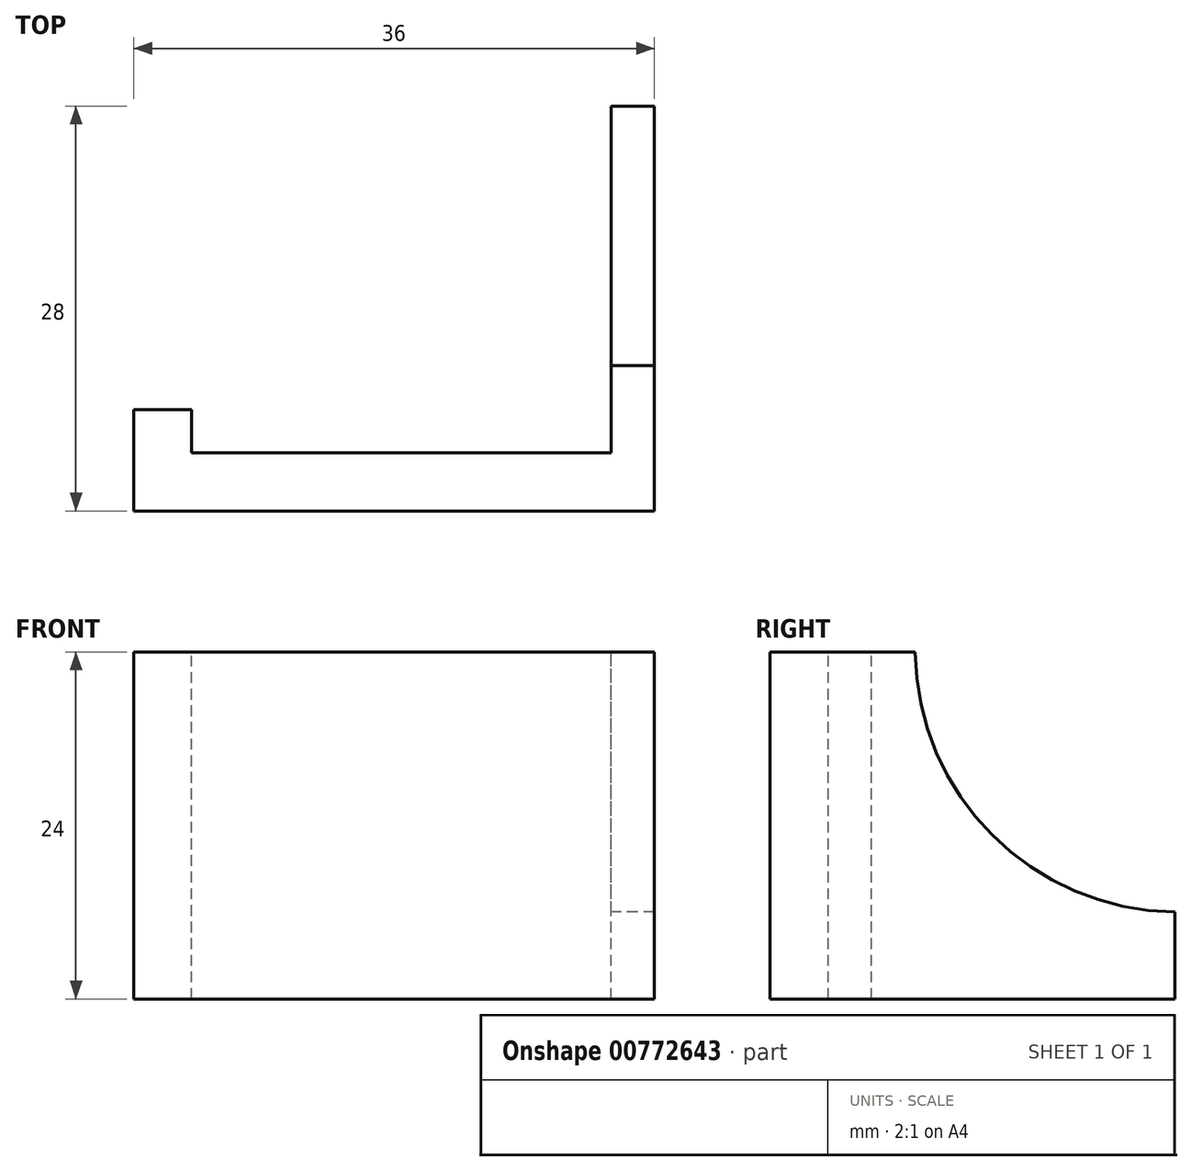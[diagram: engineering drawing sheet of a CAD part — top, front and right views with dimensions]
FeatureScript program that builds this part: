
annotation { "Feature Type Name" : "Feature", "Feature Type Description" : "" }
export const myFeature = defineFeature(function(context is Context, id is Id, definition is map)
    precondition{}
    {
        {
            var Q0;
            Q0=qCreatedBy(makeId("Right.planeOp"),FACE);
            var sketch = newSketch(context, id + "F0", { "sketchPlane" : qUnion([Q0])});
            skLineSegment(sketch, "E0", {"start": v(-23.8, 44.3) * mm, "end": v(0.2, 44.3) * mm});
            skLineSegment(sketch, "E1", {"start": v(-23.8, 44.3) * mm, "end": v(-23.8, 20.3) * mm});
            skLineSegment(sketch, "E2", {"start": v(-23.8, 20.3) * mm, "end": v(-19.76, 20.3) * mm});
            skLineSegment(sketch, "E3", {"start": v(-19.76, 20.3) * mm, "end": v(-17.76, 20.3) * mm});
            skLineSegment(sketch, "E4", {"start": v(0.2, 44.3) * mm, "end": v(0.2, 38.28) * mm});
            skArc(sketch, "E5", {"start": v(0.2, 38.28) * mm, "mid": v(-12.44, 32.94) * mm, "end": v(-17.76, 20.3) * mm});
            skSolve(sketch);
        }
        {
            var Q0;
            Q0=makeQuery(id+"F0.imprint","IMPRINT",FACE,{"disambiguationData":[TD([[makeQuery(id+"F0.imprint","IMPRINT",EDGE,{"derivedFrom":sQuery(id+"F0.wireOp",EDGE,"E0")}),-1.0]])]});
            extrude(context, id + "F1", {"entities" : qUnion([Q0]), "depth" : 3 * mm, "offsetDistance" : 25 * mm});
        }
        {
            var Q0;
            Q0=makeQuery(id+"F1.opExtrude","SWEPT_FACE",FACE,{"disambiguationData":[OSD([sQuery(id+"F0.wireOp",EDGE,"E1")])]});
            extrude(context, id + "F2", {"entities" : qUnion([Q0]), "operationType" : NewBodyOperationType.ADD, "depth" : 4 * mm, "offsetDistance" : 25 * mm});
        }
        {
            var Q0;
            {var subQ0=sQuery(id+"F0.wireOp",EDGE,"E1");Q0=makeQuery(id+"F2.boolean.opBoolean","MERGE",FACE,{"derivedFrom":[makeQuery(id+"F1.opExtrude","CAP_FACE",FACE,{"disambiguationData":[OSD([sQuery(id+"F0.wireOp",EDGE,"E0"),subQ0,sQuery(id+"F0.wireOp",EDGE,"E2"),sQuery(id+"F0.wireOp",EDGE,"hRtY1aQG-A8Zh-szPu-RmAq-oDse8q4H1be6"),sQuery(id+"F0.wireOp",EDGE,"Tq682J4d-pl9S-xHzb-lzca-EFFe5oxrAv54")])],"isStart":true}),makeQuery(id+"F2.opExtrude","SWEPT_FACE",FACE,{"disambiguationData":[OSD([subQ0]),TDD([makeQuery(id+"F1.opExtrude","CAP_EDGE",EDGE,{"disambiguationData":[OSD([subQ0])],"isStart":true})])]})]});}
            var sketch = newSketch(context, id + "F3", { "sketchPlane" : qUnion([Q0])});
            skLineSegment(sketch, "E6.bottom", {"start": v(27.8, 44.3) * mm, "end": v(23.78, 44.3) * mm});
            skLineSegment(sketch, "E6.top", {"start": v(27.8, 20.3) * mm, "end": v(23.78, 20.3) * mm});
            skLineSegment(sketch, "E6.left", {"start": v(27.8, 44.3) * mm, "end": v(27.8, 20.3) * mm});
            skLineSegment(sketch, "E6.right", {"start": v(23.78, 44.3) * mm, "end": v(23.78, 20.3) * mm});
            skSolve(sketch);
        }
        {
            var Q0;
            Q0=makeQuery(id+"F3.imprint","IMPRINT",FACE,{"disambiguationData":[TD([[makeQuery(id+"F3.imprint","IMPRINT",EDGE,{"derivedFrom":sQuery(id+"F3.wireOp",EDGE,"E6.bottom")}),1.0]])]});
            extrude(context, id + "F4", {"entities" : qUnion([Q0]), "operationType" : NewBodyOperationType.ADD, "depth" : 29 * mm, "offsetDistance" : 25 * mm});
        }
        {
            var Q0;
            Q0=makeQuery(id+"F4.opExtrude","CAP_FACE",FACE,{"disambiguationData":[OSD([sQuery(id+"F3.wireOp",EDGE,"E6.bottom"),sQuery(id+"F3.wireOp",EDGE,"E6.top"),sQuery(id+"F3.wireOp",EDGE,"E6.left"),sQuery(id+"F3.wireOp",EDGE,"E6.right")])],"isStart":false});
            extrude(context, id + "F5", {"entities" : qUnion([Q0]), "operationType" : NewBodyOperationType.ADD, "depth" : 4 * mm, "offsetDistance" : 25 * mm});
        }
        {
            var Q0;
            {var subQ0=sQuery(id+"F3.wireOp",EDGE,"E6.right");Q0=makeQuery(id+"F5.boolean.opBoolean","MERGE",FACE,{"derivedFrom":[makeQuery(id+"F4.opExtrude","SWEPT_FACE",FACE,{"disambiguationData":[OSD([subQ0])]}),makeQuery(id+"F5.opExtrude","SWEPT_FACE",FACE,{"disambiguationData":[OSD([subQ0])]})]});}
            var sketch = newSketch(context, id + "F6", { "sketchPlane" : qUnion([Q0])});
            skLineSegment(sketch, "E7.bottom", {"start": v(33, 44.3) * mm, "end": v(29, 44.3) * mm});
            skLineSegment(sketch, "E7.top", {"start": v(33, 20.3) * mm, "end": v(29, 20.3) * mm});
            skLineSegment(sketch, "E7.left", {"start": v(33, 44.3) * mm, "end": v(33, 20.3) * mm});
            skLineSegment(sketch, "E7.right", {"start": v(29, 44.3) * mm, "end": v(29, 20.3) * mm});
            skSolve(sketch);
        }
        {
            var Q0;
            Q0=makeQuery(id+"F6.imprint","IMPRINT",FACE,{"disambiguationData":[TD([[makeQuery(id+"F6.imprint","IMPRINT",EDGE,{"derivedFrom":sQuery(id+"F6.wireOp",EDGE,"E7.bottom")}),1.0]])]});
            extrude(context, id + "F7", {"entities" : qUnion([Q0]), "operationType" : NewBodyOperationType.ADD, "depth" : 3 * mm, "offsetDistance" : 25 * mm});
        }
        {
            var Q0;
            Q0=makeQuery(id+"F1.opExtrude","SWEPT_BODY",BODY,{"disambiguationData":[OSD([sQuery(id+"F0.wireOp",EDGE,"E0"),sQuery(id+"F0.wireOp",EDGE,"E1"),sQuery(id+"F0.wireOp",EDGE,"E2"),sQuery(id+"F0.wireOp",EDGE,"E3"),sQuery(id+"F0.wireOp",EDGE,"E4"),sQuery(id+"F0.wireOp",EDGE,"E5")])]});
            var Q1;
            Q1=qCreatedBy(makeId("Top.planeOp"),FACE);
            mirror(context, id + "F8", {"entities" : qUnion([Q0]), "mirrorPlane" : qUnion([Q1])});
        }
        {
            var Q0;
            Q0=makeQuery(id+"F1.opExtrude","SWEPT_BODY",BODY,{"disambiguationData":[OSD([sQuery(id+"F0.wireOp",EDGE,"E0"),sQuery(id+"F0.wireOp",EDGE,"E1"),sQuery(id+"F0.wireOp",EDGE,"E2"),sQuery(id+"F0.wireOp",EDGE,"E3"),sQuery(id+"F0.wireOp",EDGE,"E4"),sQuery(id+"F0.wireOp",EDGE,"E5")])]});
            deleteBodies(context, id + "F9", {"entities" : qUnion([Q0])});
        }
    });
